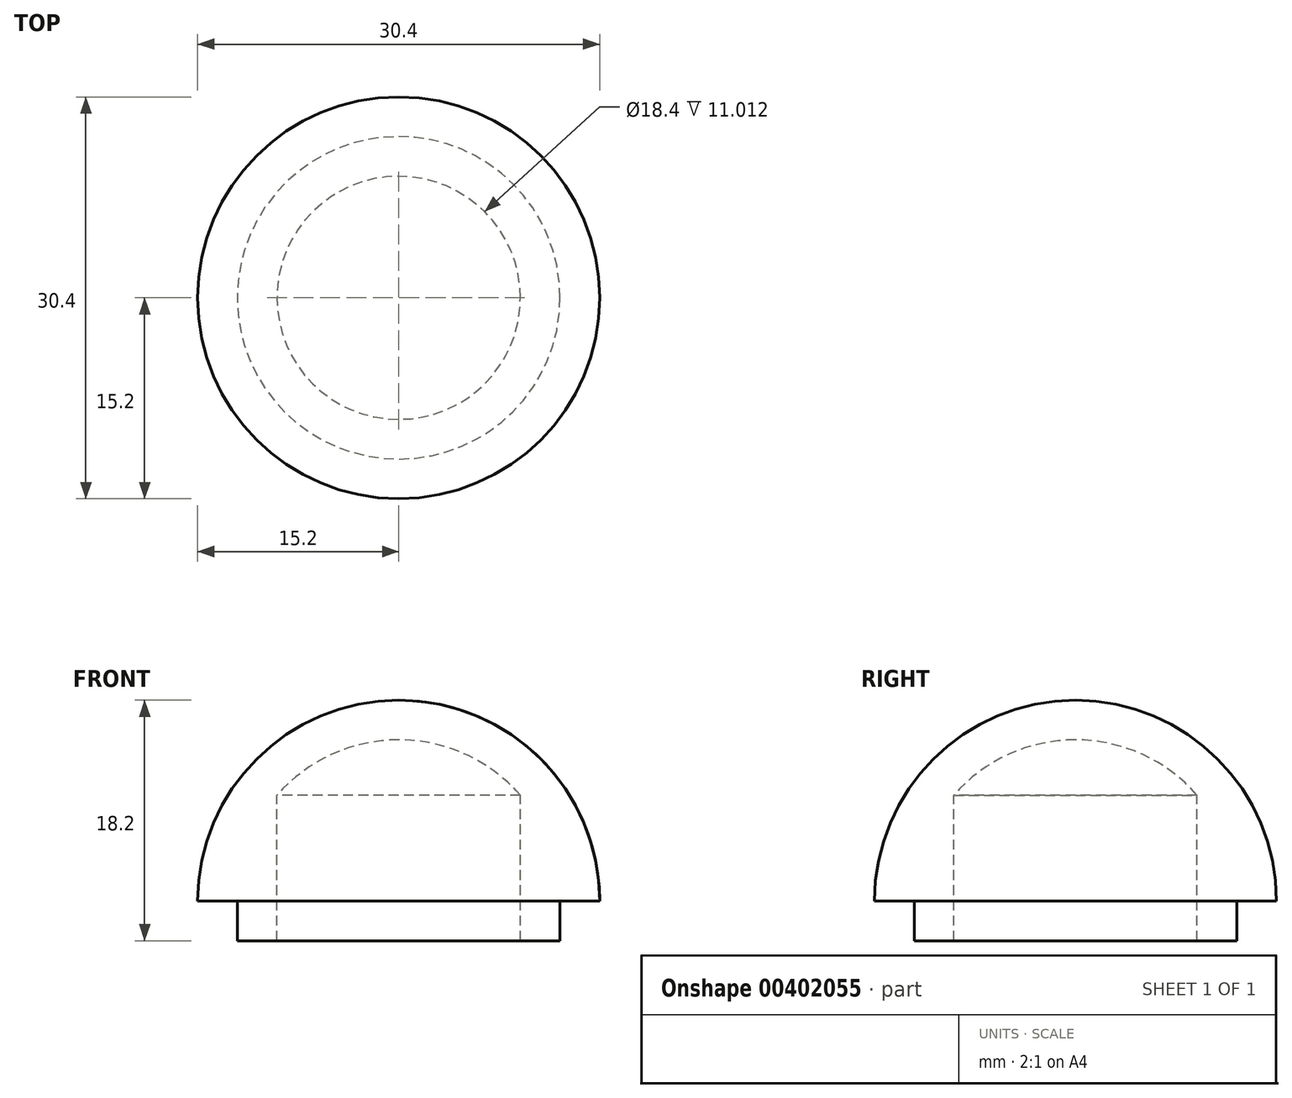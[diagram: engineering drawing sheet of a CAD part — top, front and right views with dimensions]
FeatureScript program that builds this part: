
annotation { "Feature Type Name" : "Feature", "Feature Type Description" : "" }
export const myFeature = defineFeature(function(context is Context, id is Id, definition is map)
    precondition{}
    {
        {
            var Q0;
            Q0=qCreatedBy(makeId("Front.planeOp"),FACE);
            var sketch = newSketch(context, id + "F0", { "sketchPlane" : qUnion([Q0])});
            skLineSegment(sketch, "E0", {"start": v(9.2, 0) * mm, "end": v(12.2, 0) * mm});
            skLineSegment(sketch, "E1", {"start": v(12.2, 0) * mm, "end": v(12.2, 3) * mm});
            skLineSegment(sketch, "E2", {"start": v(12.2, 3) * mm, "end": v(15.2, 3) * mm});
            skArc(sketch, "E3", {"start": v(15.2, 3) * mm, "mid": v(10.75, 13.75) * mm, "end": v(0, 18.2) * mm});
            skLineSegment(sketch, "E4", {"start": v(0, 18.2) * mm, "end": v(0, 15.2) * mm});
            skArc(sketch, "E5.0", {"start": v(9.2, 11.01) * mm, "mid": v(5.05, 14.1) * mm, "end": v(0, 15.2) * mm});
            skLineSegment(sketch, "E6", {"start": v(9.2, 0) * mm, "end": v(9.2, 11.01) * mm});
            skPoint(sketch, "E7.orphan", {"position": v(0, 0) * mm});
            skSolve(sketch);
        }
        {
            var Q0;
            Q0=makeQuery(id+"F0.imprint","IMPRINT",FACE,{"disambiguationData":[TD([[makeQuery(id+"F0.imprint","IMPRINT",EDGE,{"derivedFrom":sQuery(id+"F0.wireOp",EDGE,"E0")}),1.0]])]});
            var Q1;
            Q1=sQuery(id+"F0.wireOp",EDGE,"E4");
            revolve(context, id + "F1", {"entities" : qUnion([Q0]), "axis" : qUnion([Q1]), "revolveType" : RevolveType.FULL});
        }
    });
